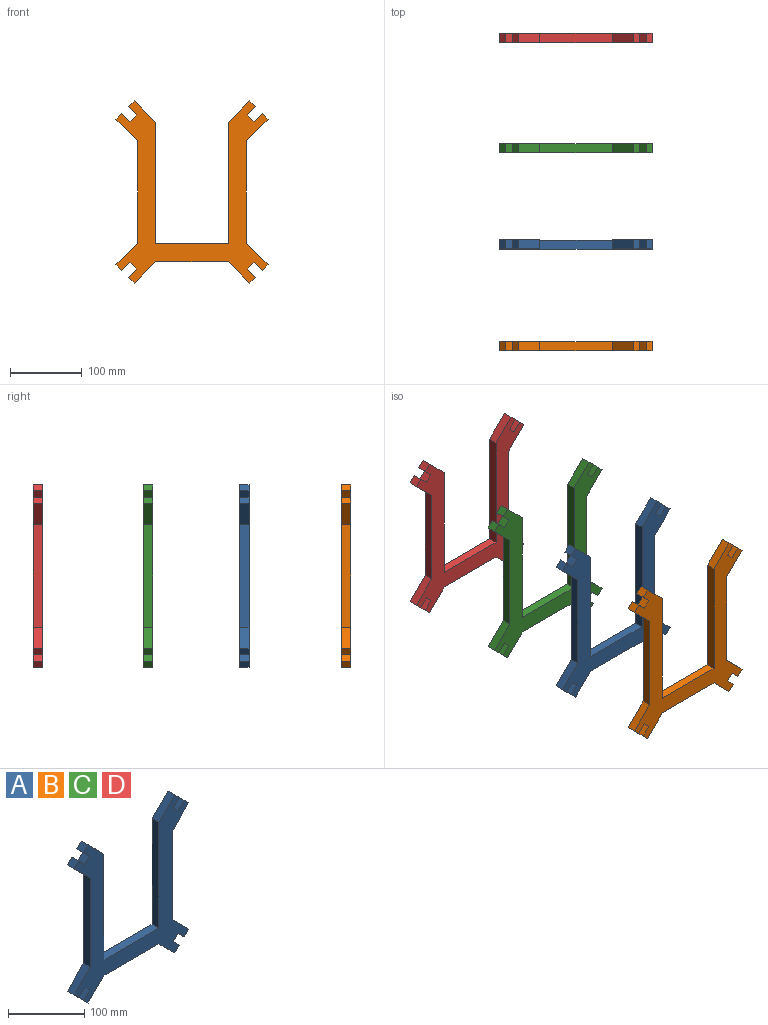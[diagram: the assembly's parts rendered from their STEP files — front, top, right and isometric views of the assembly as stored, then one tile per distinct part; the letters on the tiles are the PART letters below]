
ASSEMBLY  parts=4 mates=7
PART A: 36 faces, bbox 212.7x12.7x254.6 mm
  f0: plane 12.7x8.38mm, normal (0.71,0,-0.71), area 150.5mm2, adj f1,f33,f34,f35
  f1: plane 12.7x11.23mm, normal (0.71,0,0.71), area 201.6mm2, adj f0,f2,f34,f35
  f2: plane 12.7x8.98mm, normal (0.71,0,-0.71), area 161.3mm2, adj f1,f3,f34,f35
  f3: plane 12.7x11.23mm, normal (-0.71,0,-0.71), area 201.6mm2, adj f2,f4,f34,f35
  f4: plane 12.7x8.38mm, normal (0.71,0,-0.71), area 150.5mm2, adj f3,f5,f34,f35
  f5: plane 30.23x30.23mm, normal (0.71,0,0.71), area 543mm2, adj f4,f6,f34,f35
  f6: plane 142.64x12.7mm, normal (1,0,0), area 1811.5mm2, adj f5,f7,f34,f35
  f7: plane 30.23x30.23mm, normal (0.71,0,-0.71), area 543mm2, adj f6,f8,f34,f35
  f8: plane 12.7x8.38mm, normal (0.71,0,0.71), area 150.5mm2, adj f7,f9,f34,f35
  f9: plane 12.7x11.23mm, normal (-0.71,0,0.71), area 201.6mm2, adj f8,f10,f34,f35
  f10: plane 12.7x8.98mm, normal (0.71,0,0.71), area 161.3mm2, adj f9,f11,f34,f35
  f11: plane 12.7x11.23mm, normal (0.71,0,-0.71), area 201.6mm2, adj f10,f12,f34,f35
  f12: plane 12.7x8.38mm, normal (0.71,0,0.71), area 150.5mm2, adj f11,f13,f34,f35
  f13: plane 29.58x29.58mm, normal (-0.71,0,0.71), area 531.2mm2, adj f12,f14,f34,f35
  f14: plane 170.34x12.7mm, normal (-1,0,0), area 2163.3mm2, adj f13,f15,f34,f35
  f15: plane 102.03x12.7mm, normal (0,0,1), area 1295.8mm2, adj f14,f16,f34,f35
  f16: plane 170.34x12.7mm, normal (1,0,0), area 2163.3mm2, adj f15,f17,f34,f35
  f17: plane 29.58x29.58mm, normal (0.71,0,0.71), area 531.2mm2, adj f16,f18,f34,f35
  f18: plane 12.7x8.38mm, normal (-0.71,0,0.71), area 150.5mm2, adj f17,f19,f34,f35
  f19: plane 12.7x11.23mm, normal (-0.71,0,-0.71), area 201.6mm2, adj f18,f20,f34,f35
  f20: plane 12.7x8.98mm, normal (-0.71,0,0.71), area 161.3mm2, adj f19,f21,f34,f35
  f21: plane 12.7x11.23mm, normal (0.71,0,0.71), area 201.6mm2, adj f20,f22,f34,f35
  f22: plane 12.7x8.38mm, normal (-0.71,0,0.71), area 150.5mm2, adj f21,f23,f34,f35
  f23: plane 30.23x30.23mm, normal (-0.71,0,-0.71), area 543mm2, adj f22,f24,f34,f35
  f24: plane 142.64x12.7mm, normal (-1,0,0), area 1811.5mm2, adj f23,f25,f34,f35
  f25: plane 30.23x30.23mm, normal (-0.71,0,0.71), area 543mm2, adj f24,f26,f34,f35
  f26: plane 12.7x8.38mm, normal (-0.71,0,-0.71), area 150.5mm2, adj f25,f27,f34,f35
  f27: plane 12.7x11.23mm, normal (0.71,0,-0.71), area 201.6mm2, adj f26,f28,f34,f35
  f28: plane 12.7x8.98mm, normal (-0.71,0,-0.71), area 161.3mm2, adj f27,f29,f34,f35
  f29: plane 12.7x11.23mm, normal (-0.71,0,0.71), area 201.6mm2, adj f28,f30,f34,f35
  f30: plane 12.7x8.38mm, normal (-0.71,0,-0.71), area 150.5mm2, adj f29,f31,f34,f35
  f31: plane 29.58x29.58mm, normal (0.71,0,-0.71), area 531.2mm2, adj f30,f32,f34,f35
  f32: plane 102.03x12.7mm, normal (0,0,-1), area 1295.8mm2, adj f31,f33,f34,f35
  f33: plane 29.58x29.58mm, normal (-0.71,0,-0.71), area 531.2mm2, adj f0,f32,f34,f35
  f34: plane 254.57x212.65mm, normal (0,-1,0), area 16387.9mm2, adj f0,f1,f2,f3,f4,f5,f6,f7
  f35: plane 254.57x212.65mm, normal (0,1,0), area 16387.9mm2, adj f0,f1,f2,f3,f4,f5,f6,f7
PART B: same geometry as A
PART C: same geometry as A
PART D: same geometry as A
PLACE A t=(-160.72,-133.34,-7.26)mm
PLACE B t=(-160.72,-275.48,-7.26)mm
PLACE C t=(-160.72,1.16,-7.26)mm
PLACE D t=(-160.72,155.48,-7.26)mm
MATE planar A.f15 <-> B.f15  axis (0,0,1) through (-160.72,-133.34,-79.89)mm
MATE planar D.f15 <-> C.f15  axis (0,0,1) through (-160.72,155.48,-79.89)mm
MATE planar D.f15 <-> A.f15  axis (0,0,1) through (-160.72,155.48,-79.89)mm
MATE planar C.f6 <-> A.f6  axis (1,0,0) through (-84.63,1.16,-7.26)mm
MATE planar D.f6 <-> C.f6  axis (1,0,0) through (-84.63,155.48,-7.26)mm
MATE planar C.f6 <-> B.f6  axis (1,0,0) through (-84.63,1.16,-7.26)mm
MATE planar D.f6 <-> A.f6  axis (1,0,0) through (-84.63,155.48,-7.26)mm
